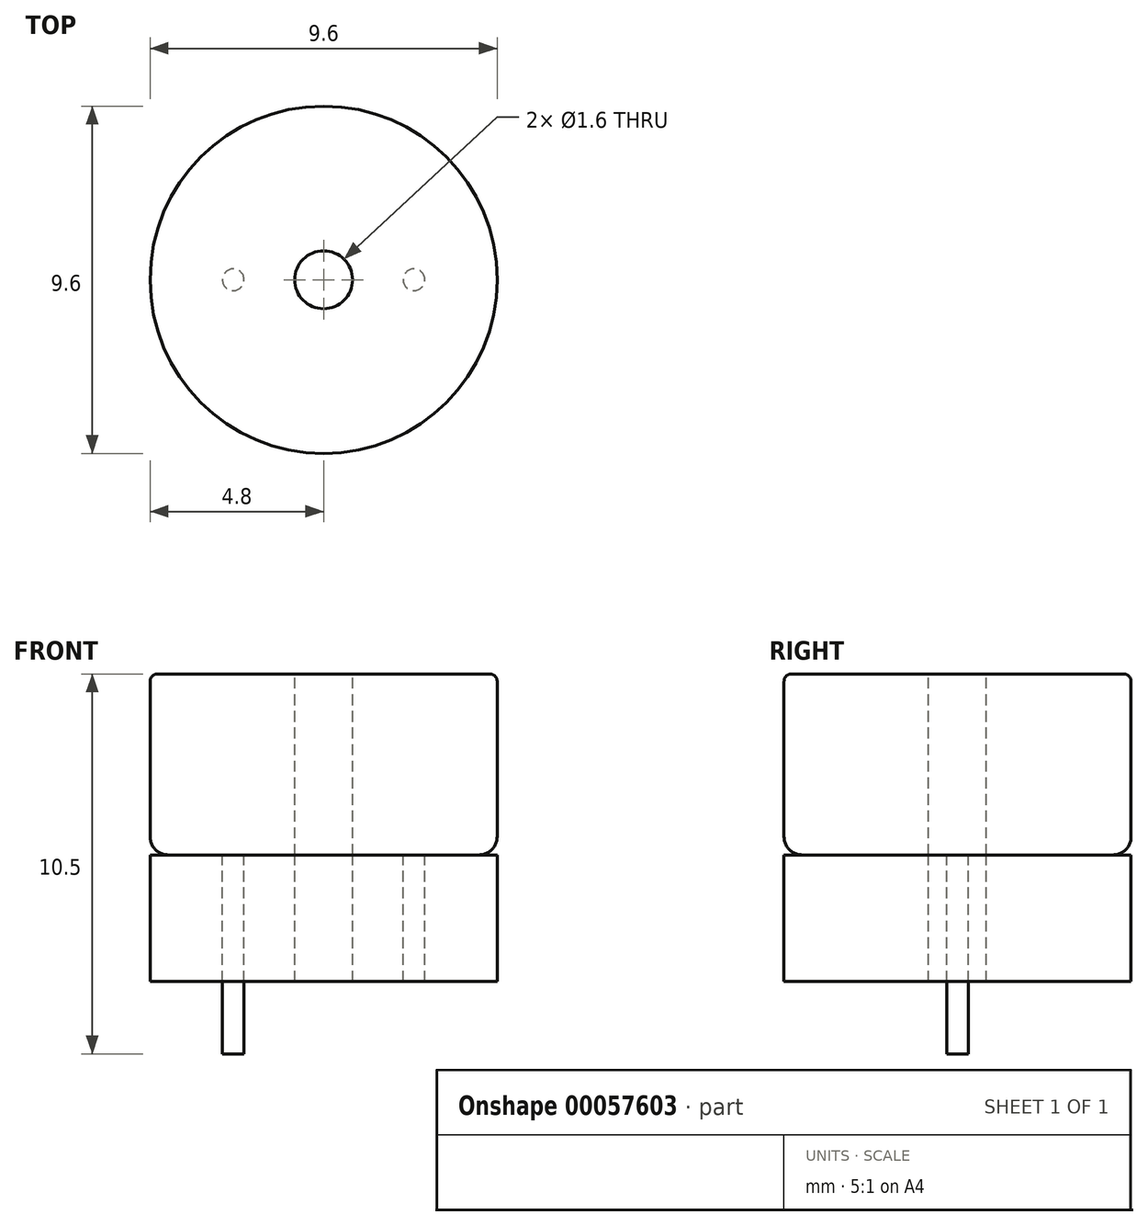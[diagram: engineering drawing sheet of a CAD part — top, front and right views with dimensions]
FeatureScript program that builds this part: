
annotation { "Feature Type Name" : "Feature", "Feature Type Description" : "" }
export const myFeature = defineFeature(function(context is Context, id is Id, definition is map)
    precondition{}
    {
        {
            var Q0;
            Q0=qCreatedBy(makeId("Top.planeOp"),FACE);
            var sketch = newSketch(context, id + "F0", { "sketchPlane" : qUnion([Q0])});
            skCircle(sketch, "E0", {"center": v(0, 0) * mm, "radius": 4.8 * mm});
            skCircle(sketch, "E1", {"center": v(0, 0) * mm, "radius": 4.55 * mm});
            skSolve(sketch);
        }
        {
            var Q0;
            Q0=makeQuery(id+"F0.imprint","IMPRINT",FACE,{"disambiguationData":[TD([[makeQuery(id+"F0.imprint","IMPRINT",EDGE,{"derivedFrom":sQuery(id+"F0.wireOp",EDGE,"E0")}),1.0]])]});
            extrude(context, id + "F1", {"entities" : qUnion([Q0]), "depth" : 4.5 * mm});
        }
        {
            var Q0;
            Q0=makeQuery(id+"F1.opExtrude","CAP_FACE",FACE,{"disambiguationData":[OSD([sQuery(id+"F0.wireOp",EDGE,"E0"),sQuery(id+"F0.wireOp",EDGE,"E1")])],"isStart":false});
            var sketch = newSketch(context, id + "F2", { "sketchPlane" : qUnion([Q0])});
            skCircle(sketch, "E2", {"center": v(0, 0) * mm, "radius": 4.55 * mm});
            skPoint(sketch, "E2.first.point", {"position": v(0.12, -4.55) * mm});
            skPoint(sketch, "E2.second.point", {"position": v(-4.06, 2.05) * mm});
            skPoint(sketch, "E2.third.point", {"position": v(1.27, 4.37) * mm});
            skSolve(sketch);
        }
        {
            var Q0;
            Q0 = qSketchRegion(id + "F2", true);
            extrude(context, id + "F3", {"entities" : qUnion([Q0]), "oppositeDirection" : true, "depth" : .5 * mm});
        }
        {
            var Q0;
            Q0=makeQuery(id+"F1.opExtrude","CAP_FACE",FACE,{"disambiguationData":[OSD([sQuery(id+"F0.wireOp",EDGE,"E0"),sQuery(id+"F0.wireOp",EDGE,"E1")])],"isStart":false});
            var sketch = newSketch(context, id + "F4", { "sketchPlane" : qUnion([Q0])});
            skCircle(sketch, "E3", {"center": v(0, 0) * mm, "radius": 4.8 * mm});
            skPoint(sketch, "E3.first.point", {"position": v(-1.67, -4.5) * mm});
            skPoint(sketch, "E3.second.point", {"position": v(-2.06, 4.33) * mm});
            skPoint(sketch, "E3.third.point", {"position": v(4.46, 1.76) * mm});
            skSolve(sketch);
        }
        {
            var Q0;
            Q0 = qSketchRegion(id + "F4", true);
            extrude(context, id + "F5", {"entities" : qUnion([Q0]), "operationType" : NewBodyOperationType.ADD, "depth" : .5 * mm});
        }
        {
            var Q0;
            Q0=makeQuery(id+"F5.opExtrude","CAP_FACE",FACE,{"disambiguationData":[OSD([sQuery(id+"F4.wireOp",EDGE,"E3")])],"isStart":false});
            var sketch = newSketch(context, id + "F6", { "sketchPlane" : qUnion([Q0])});
            skCircle(sketch, "E4", {"center": v(0, 0) * mm, "radius": 0.8 * mm});
            skSolve(sketch);
        }
        {
            var Q0;
            Q0 = qSketchRegion(id + "F6", true);
            var Q1;
            Q1=makeQuery(id+"F6.imprint","IMPRINT",FACE,{"disambiguationData":[TD([[makeQuery(id+"F6.imprint","IMPRINT",EDGE,{"derivedFrom":sQuery(id+"F6.wireOp",EDGE,"E4")}),1.0]])]});
            extrude(context, id + "F7", {"entities" : qUnion([Q0, Q1]), "operationType" : NewBodyOperationType.REMOVE, "endBound" : BoundingType.UP_TO_NEXT, "oppositeDirection" : true, "depth" : 2 * mm});
        }
        {
            var Q0;
            Q0=makeQuery(id+"F3.opExtrude","CAP_FACE",FACE,{"disambiguationData":[OSD([sQuery(id+"F2.wireOp",EDGE,"E2")])],"isStart":false});
            extrude(context, id + "F8", {"entities" : qUnion([Q0]), "operationType" : NewBodyOperationType.ADD, "depth" : 4 * mm});
        }
        {
            var Q0;
            Q0=makeQuery(id+"F8.boolean.opBoolean","MERGE",FACE,{"derivedFrom":[makeQuery(id+"F1.opExtrude","CAP_FACE",FACE,{"disambiguationData":[OSD([sQuery(id+"F0.wireOp",EDGE,"E0"),sQuery(id+"F0.wireOp",EDGE,"E1")])],"isStart":true}),makeQuery(id+"F8.opExtrude","CAP_FACE",FACE,{"disambiguationData":[OSD([sQuery(id+"F2.wireOp",EDGE,"E2")])],"isStart":false})]});
            var sketch = newSketch(context, id + "F9", { "sketchPlane" : qUnion([Q0])});
            skCircle(sketch, "E5", {"center": v(-2.5, 0) * mm, "radius": 0.3 * mm});
            skCircle(sketch, "E6.MirrorC", {"center": v(2.5, 0) * mm, "radius": 0.3 * mm});
            skSolve(sketch);
        }
        {
            var Q0;
            Q0=makeQuery(id+"F9.imprint","IMPRINT",FACE,{"disambiguationData":[TD([[makeQuery(id+"F9.imprint","IMPRINT",EDGE,{"derivedFrom":sQuery(id+"F9.wireOp",EDGE,"E5")}),1.0]])]});
            extrude(context, id + "F10", {"entities" : qUnion([Q0]), "depth" : 5.5 * mm});
        }
        {
            var Q0;
            Q0=makeQuery(id+"F9.imprint","IMPRINT",FACE,{"disambiguationData":[TD([[makeQuery(id+"F9.imprint","IMPRINT",EDGE,{"derivedFrom":sQuery(id+"F9.wireOp",EDGE,"E6.MirrorC")}),-1.0]])]});
            extrude(context, id + "F11", {"entities" : qUnion([Q0]), "depth" : 3.5 * mm});
        }
        {
            var Q0;
            Q0=makeQuery(id+"F5.opExtrude","CAP_EDGE",EDGE,{"disambiguationData":[OSD([sQuery(id+"F4.wireOp",EDGE,"E3")])],"isStart":false});
            fillet(context, id + "F12", {"entities" : qUnion([Q0]), "radius" : .2 * mm, "tangentPropagation" : true, "allowEdgeOverflow" : false});
        }
        {
            var Q0;
            Q0=makeQuery(id+"F1.opExtrude","CAP_EDGE",EDGE,{"disambiguationData":[OSD([sQuery(id+"F0.wireOp",EDGE,"E0")])],"isStart":true});
            fillet(context, id + "F13", {"entities" : qUnion([Q0]), "radius" : .5 * mm, "tangentPropagation" : true, "allowEdgeOverflow" : false});
        }
    });
